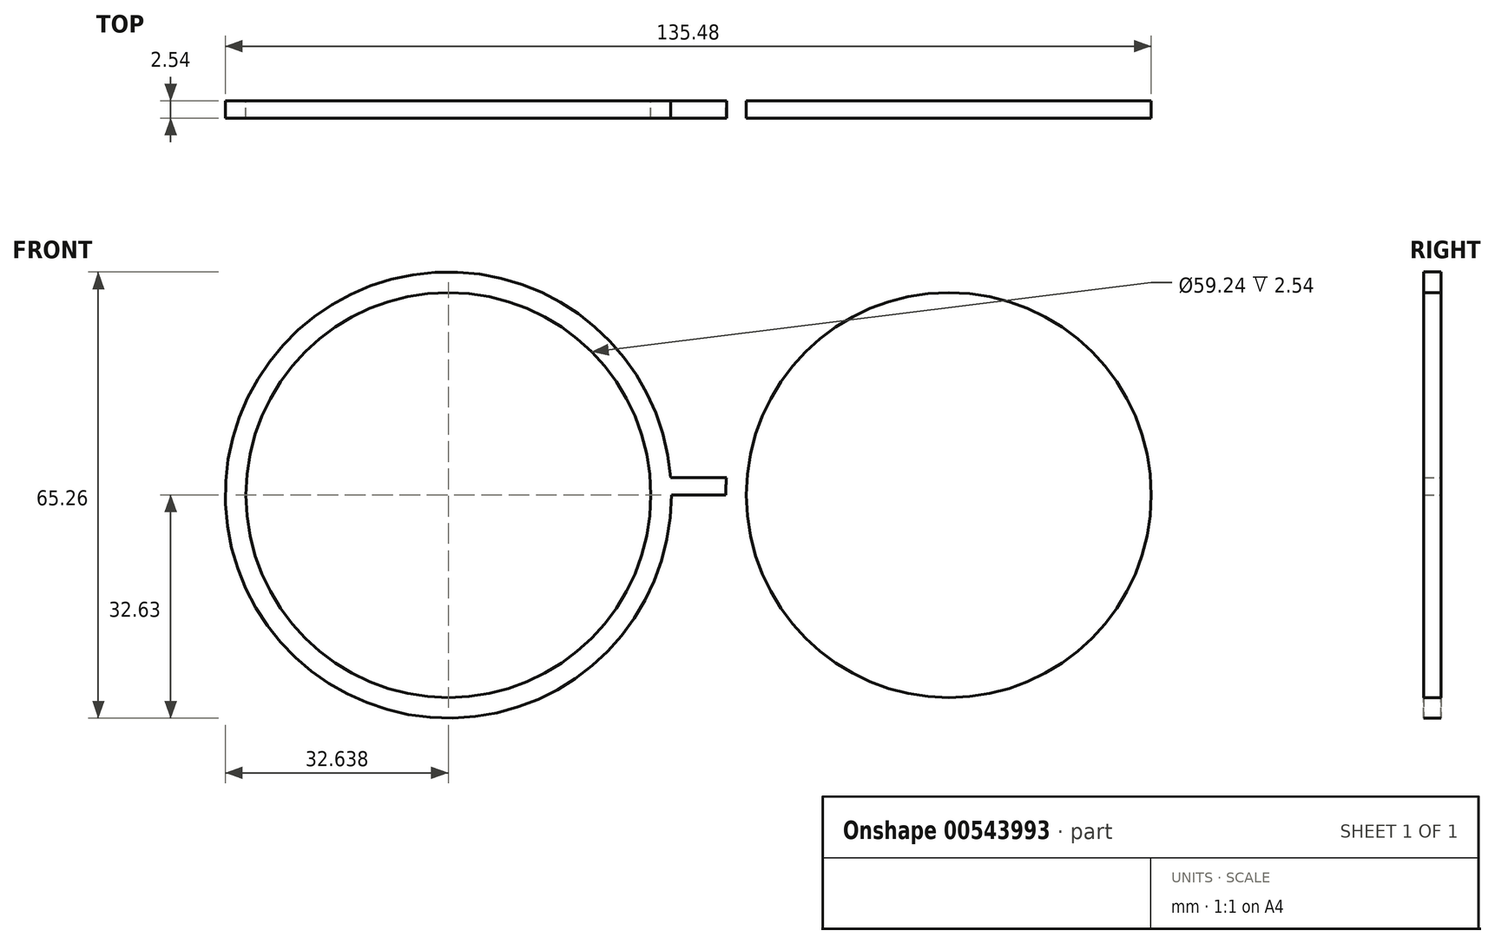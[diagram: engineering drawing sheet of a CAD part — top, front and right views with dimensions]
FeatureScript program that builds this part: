
annotation { "Feature Type Name" : "Feature", "Feature Type Description" : "" }
export const myFeature = defineFeature(function(context is Context, id is Id, definition is map)
    precondition{}
    {
        {
            var Q0;
            Q0=qCreatedBy(makeId("Front.planeOp"),FACE);
            var sketch = newSketch(context, id + "F0", { "sketchPlane" : qUnion([Q0])});
            skCircle(sketch, "E0", {"center": v(-36.61, 0) * mm, "radius": 32.63 * mm});
            skCircle(sketch, "E1", {"center": v(-36.61, 0) * mm, "radius": 29.62 * mm});
            skCircle(sketch, "E2.MirrorC", {"center": v(36.61, 0) * mm, "radius": 29.62 * mm});
            skCircle(sketch, "E3.MirrorC", {"center": v(36.61, 0) * mm, "radius": 32.63 * mm});
            skLineSegment(sketch, "E4", {"start": v(-4.08, 2.56) * mm, "end": v(0, 2.56) * mm});
            skLineSegment(sketch, "E5", {"start": v(-3.98, 0) * mm, "end": v(0, 0) * mm});
            skLineSegment(sketch, "E6.MirrorCS", {"start": v(4.08, 2.56) * mm, "end": v(0, 2.56) * mm});
            skLineSegment(sketch, "E7.MirrorCS", {"start": v(3.98, 0) * mm, "end": v(0, 0) * mm});
            skSolve(sketch);
        }
        {
            var Q0;
            Q0=makeQuery(id+"F0.imprint","IMPRINT",FACE,{"disambiguationData":[TD([[makeQuery(id+"F0.imprint","IMPRINT",EDGE,{"derivedFrom":sQuery(id+"F0.wireOp",EDGE,"E1")}),-1.0]])]});
            var Q1;
            {var subQ1=sQuery(id+"F0.wireOp",EDGE,"E4");Q1=makeQuery(id+"F0.imprint","IMPRINT",FACE,{"disambiguationData":[TD([[makeQuery(id+"F0.imprint","IMPRINT",EDGE,{"derivedFrom":subQ1}),-1.0]])]});}
            var Q2;
            Q2=makeQuery(id+"F0.imprint","IMPRINT",FACE,{"disambiguationData":[TD([[makeQuery(id+"F0.imprint","IMPRINT",EDGE,{"derivedFrom":sQuery(id+"F0.wireOp",EDGE,"E2.MirrorC")}),1.0]])]});
            extrude(context, id + "F1", {"entities" : qUnion([Q0, Q1, Q2]), "depth" : 2.54 * mm, "offsetDistance" : 25.4 * mm});
        }
    });
